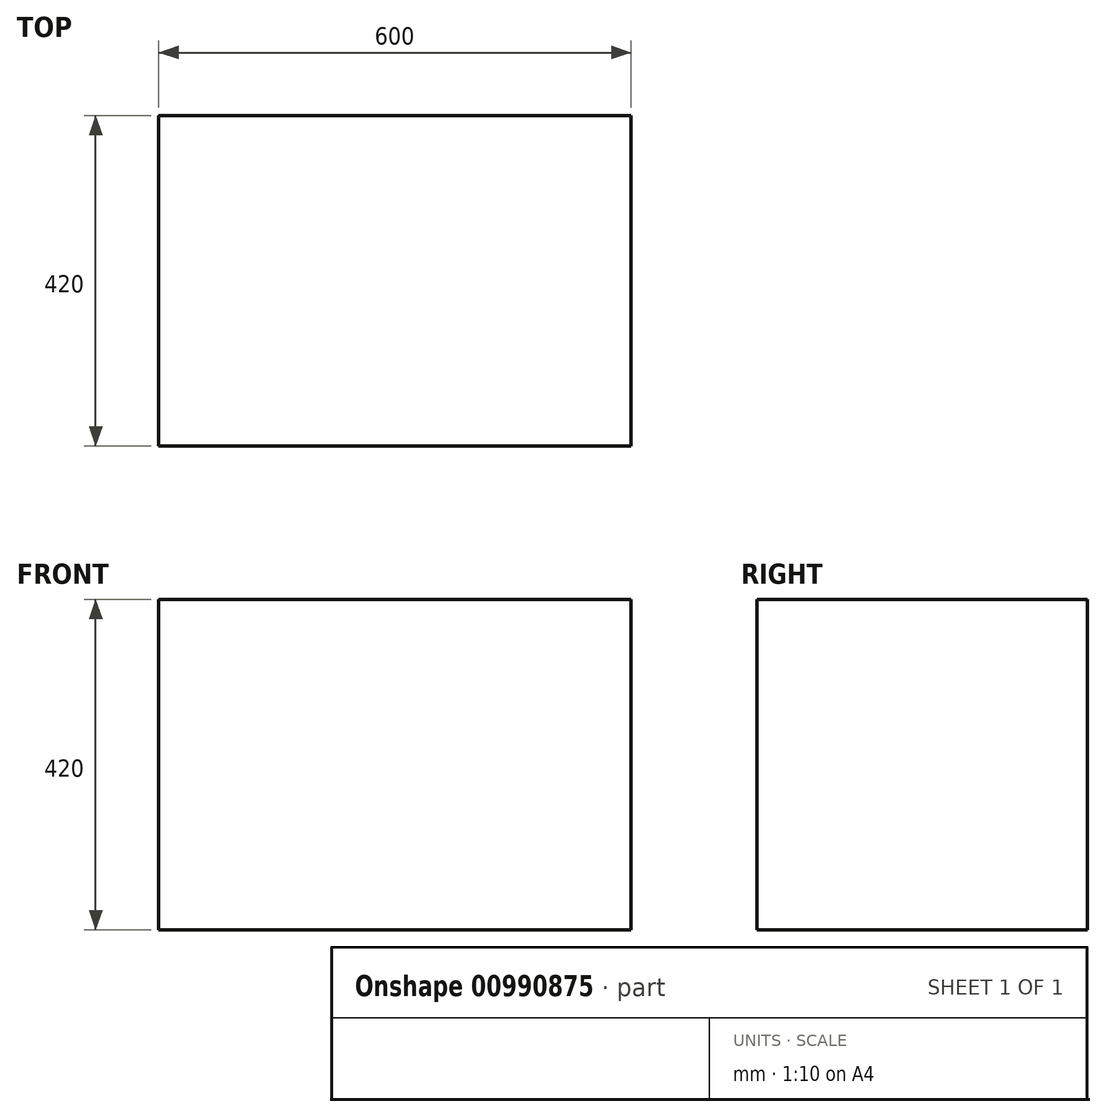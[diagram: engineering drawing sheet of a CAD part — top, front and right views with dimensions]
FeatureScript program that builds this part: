
annotation { "Feature Type Name" : "Feature", "Feature Type Description" : "" }
export const myFeature = defineFeature(function(context is Context, id is Id, definition is map)
    precondition{}
    {
        {
            var Q0;
            Q0=qCreatedBy(makeId("Top.planeOp"),FACE);
            var sketch = newSketch(context, id + "F0", { "sketchPlane" : qUnion([Q0])});
            skLineSegment(sketch, "E0", {"start": v(-106.42, -25.86) * mm, "end": v(493.58, -25.86) * mm});
            skLineSegment(sketch, "E1", {"start": v(493.58, -25.86) * mm, "end": v(493.58, 394.14) * mm});
            skLineSegment(sketch, "E2", {"start": v(493.58, 394.14) * mm, "end": v(-106.42, 394.14) * mm});
            skLineSegment(sketch, "E3", {"start": v(-106.42, 394.14) * mm, "end": v(-106.42, -25.86) * mm});
            skSolve(sketch);
        }
        {
            var Q0;
            Q0=makeQuery(id+"F0.imprint","IMPRINT",FACE,{"disambiguationData":[TD([[makeQuery(id+"F0.imprint","IMPRINT",EDGE,{"derivedFrom":sQuery(id+"F0.wireOp",EDGE,"E0")}),1.0]])]});
            extrude(context, id + "F1", {"entities" : qUnion([Q0]), "depth" : 420 * mm, "offsetDistance" : 25 * mm});
        }
    });
